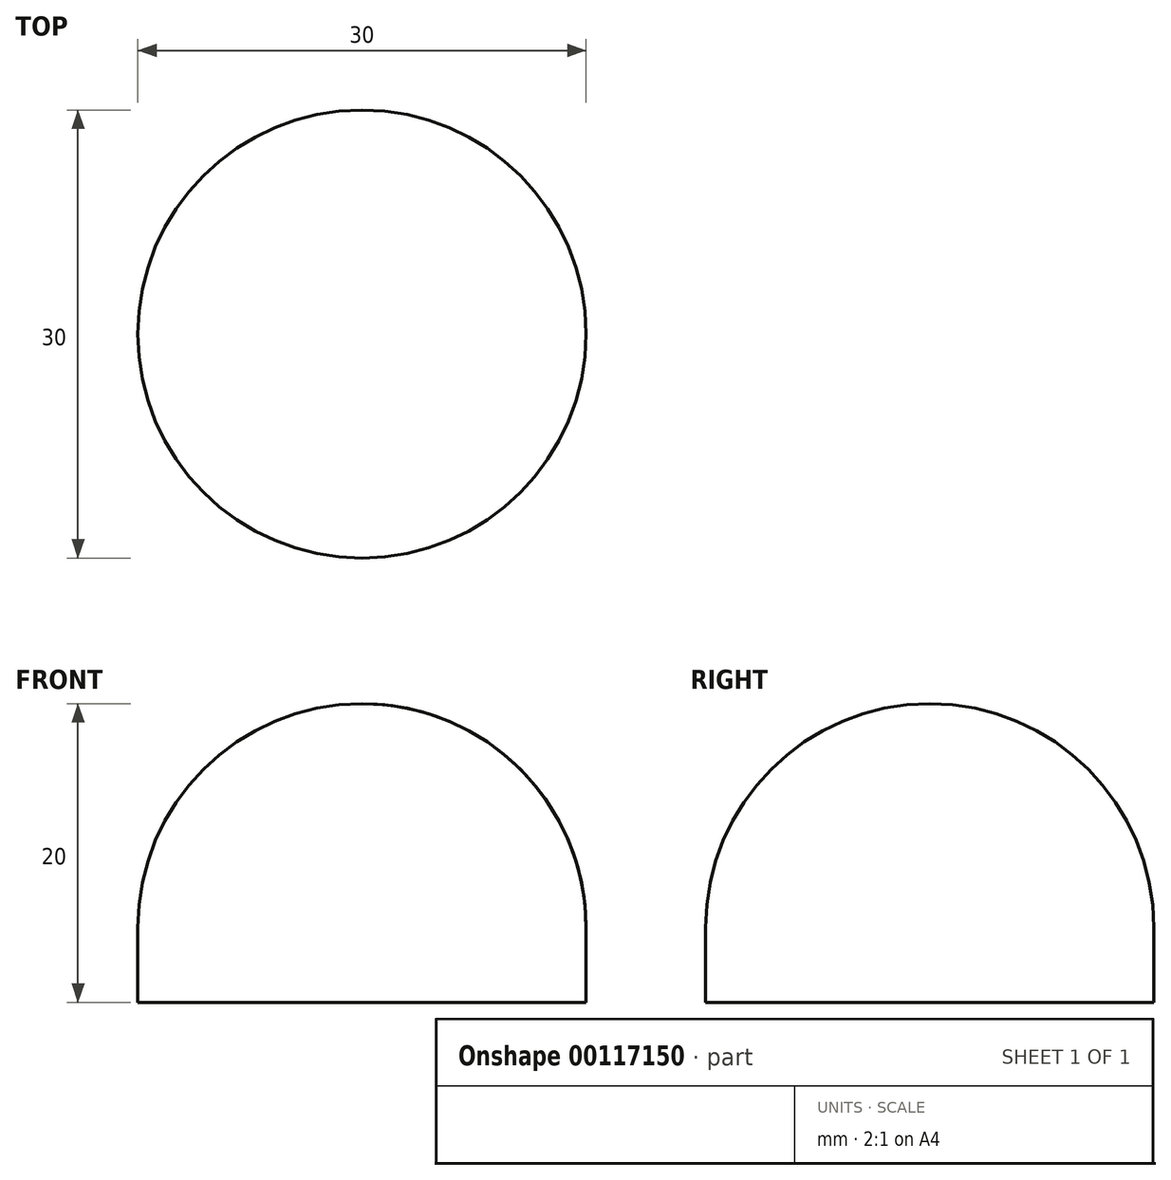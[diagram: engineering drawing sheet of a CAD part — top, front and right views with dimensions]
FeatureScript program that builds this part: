
annotation { "Feature Type Name" : "Feature", "Feature Type Description" : "" }
export const myFeature = defineFeature(function(context is Context, id is Id, definition is map)
    precondition{}
    {
        {
            var Q0;
            Q0=qCreatedBy(makeId("Front.planeOp"),FACE);
            var sketch = newSketch(context, id + "F0", { "sketchPlane" : qUnion([Q0])});
            skLineSegment(sketch, "E0", {"start": v(0, 0) * mm, "end": v(15, 0) * mm});
            skLineSegment(sketch, "E1", {"start": v(15, 0) * mm, "end": v(15, 5) * mm});
            skArc(sketch, "E2", {"start": v(15, 5) * mm, "mid": v(10.6, 15.6) * mm, "end": v(0, 20) * mm});
            skLineSegment(sketch, "E3", {"start": v(0, 20) * mm, "end": v(0, 0) * mm});
            skSolve(sketch);
        }
        {
            var Q0;
            Q0=makeQuery(id+"F0.imprint","IMPRINT",FACE,{"disambiguationData":[TD([[makeQuery(id+"F0.imprint","IMPRINT",EDGE,{"derivedFrom":sQuery(id+"F0.wireOp",EDGE,"E0")}),1.0]])]});
            var Q1;
            Q1=sQuery(id+"F0.wireOp",EDGE,"E3");
            revolve(context, id + "F1", {"entities" : qUnion([Q0]), "axis" : qUnion([Q1]), "revolveType" : RevolveType.FULL});
        }
    });
